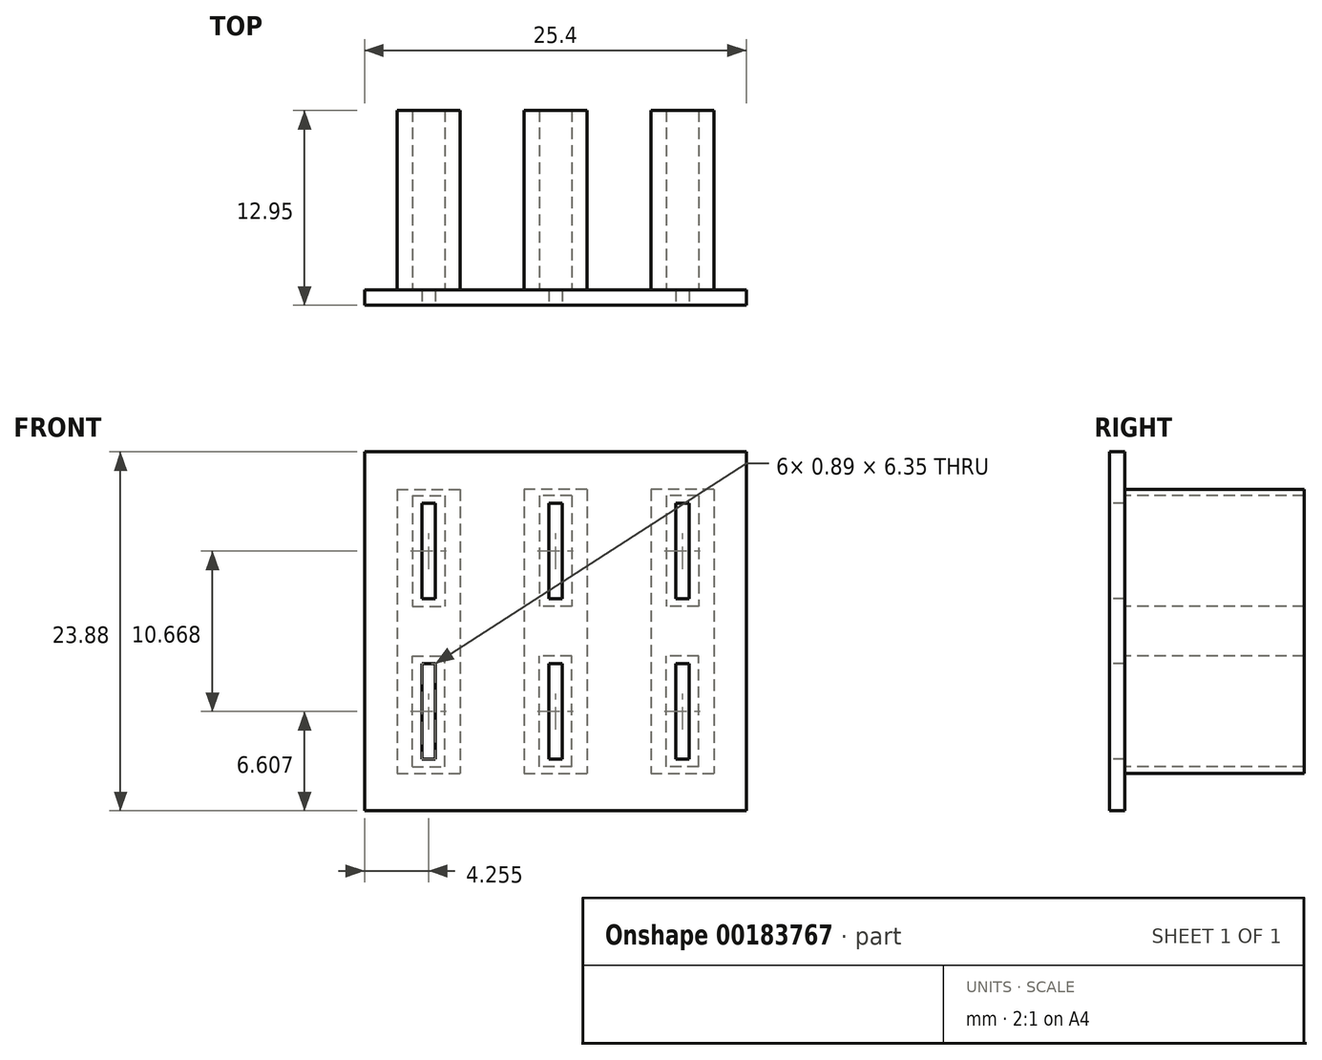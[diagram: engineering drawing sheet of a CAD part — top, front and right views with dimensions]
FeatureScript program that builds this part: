
annotation { "Feature Type Name" : "Feature", "Feature Type Description" : "" }
export const myFeature = defineFeature(function(context is Context, id is Id, definition is map)
    precondition{}
    {
        {
            var Q0;
            Q0=qCreatedBy(makeId("Front.planeOp"),FACE);
            var sketch = newSketch(context, id + "F0", { "sketchPlane" : qUnion([Q0])});
            skLineSegment(sketch, "E0.bottom", {"start": v(-12.7, 12.4) * mm, "end": v(12.7, 12.4) * mm});
            skLineSegment(sketch, "E0.top", {"start": v(-12.7, -11.47) * mm, "end": v(12.7, -11.47) * mm});
            skLineSegment(sketch, "E0.left", {"start": v(-12.7, 12.4) * mm, "end": v(-12.7, -11.47) * mm});
            skLineSegment(sketch, "E0.right", {"start": v(12.7, 12.4) * mm, "end": v(12.7, -11.47) * mm});
            skPoint(sketch, "E0.middle", {"position": v(0, 0.47) * mm});
            skLineSegment(sketch, "E1", {"start": v(0, 12.4) * mm, "end": v(0, -11.47) * mm, "construction": true});
            skLineSegment(sketch, "E2", {"start": v(0, 12.4) * mm, "end": v(-12.7, 12.4) * mm, "construction": true});
            skLineSegment(sketch, "E3", {"start": v(-8.45, 12.4) * mm, "end": v(-8.45, -11.47) * mm, "construction": true});
            skLineSegment(sketch, "E4.MirrorCS", {"start": v(8.45, 12.4) * mm, "end": v(8.45, -11.47) * mm, "construction": true});
            skLineSegment(sketch, "E5", {"start": v(-12.7, 0.47) * mm, "end": v(12.7, 0.47) * mm, "construction": true});
            skLineSegment(sketch, "E6.bottom", {"start": v(-8, 8.98) * mm, "end": v(-8.89, 8.98) * mm});
            skLineSegment(sketch, "E6.top", {"start": v(-8, 2.63) * mm, "end": v(-8.89, 2.63) * mm});
            skLineSegment(sketch, "E6.left", {"start": v(-8, 8.98) * mm, "end": v(-8, 2.63) * mm});
            skLineSegment(sketch, "E6.right", {"start": v(-8.9, 8.98) * mm, "end": v(-8.9, 2.63) * mm});
            skPoint(sketch, "E6.middle", {"position": v(-8.45, 5.8) * mm});
            skLineSegment(sketch, "E7.MirrorCS", {"start": v(8, 8.98) * mm, "end": v(8, 2.63) * mm});
            skLineSegment(sketch, "E8.MirrorCS", {"start": v(8, 8.98) * mm, "end": v(8.89, 8.98) * mm});
            skLineSegment(sketch, "E9.MirrorCS", {"start": v(8.9, 8.98) * mm, "end": v(8.9, 2.63) * mm});
            skLineSegment(sketch, "E10.MirrorCS", {"start": v(8, 2.63) * mm, "end": v(8.89, 2.63) * mm});
            skLineSegment(sketch, "E11", {"start": v(0, 12.4) * mm, "end": v(-8.45, 12.4) * mm});
            skLineSegment(sketch, "E12", {"start": v(-4.22, 12.4) * mm, "end": v(-4.22, -11.47) * mm, "construction": true});
            skLineSegment(sketch, "E13.MirrorCS", {"start": v(4.22, 12.4) * mm, "end": v(4.22, -11.47) * mm, "construction": true});
            skPoint(sketch, "E14.MirrorP", {"position": v(0, 5.8) * mm});
            skLineSegment(sketch, "E15.MirrorCS", {"start": v(0.44, 8.98) * mm, "end": v(0.44, 2.63) * mm});
            skLineSegment(sketch, "E16.MirrorCS", {"start": v(-0.44, 8.98) * mm, "end": v(-0.44, 2.63) * mm});
            skLineSegment(sketch, "E17.MirrorCS", {"start": v(-0.44, 2.63) * mm, "end": v(0.44, 2.63) * mm});
            skLineSegment(sketch, "E18.MirrorCS", {"start": v(-0.44, 8.98) * mm, "end": v(0.44, 8.98) * mm});
            skLineSegment(sketch, "E19.MirrorCS", {"start": v(8, -1.69) * mm, "end": v(8.9, -1.69) * mm});
            skLineSegment(sketch, "E20.MirrorCS", {"start": v(-0.44, -8.04) * mm, "end": v(-0.44, -1.69) * mm});
            skLineSegment(sketch, "E21.MirrorCS", {"start": v(-0.44, -1.69) * mm, "end": v(0.44, -1.69) * mm});
            skLineSegment(sketch, "E22.MirrorCS", {"start": v(-8.9, -8.04) * mm, "end": v(-8.9, -1.69) * mm});
            skLineSegment(sketch, "E23.MirrorCS", {"start": v(-8, -8.04) * mm, "end": v(-8, -1.69) * mm});
            skLineSegment(sketch, "E24.MirrorCS", {"start": v(-8, -1.69) * mm, "end": v(-8.89, -1.69) * mm});
            skLineSegment(sketch, "E25.MirrorCS", {"start": v(-8, -8.04) * mm, "end": v(-8.89, -8.04) * mm});
            skPoint(sketch, "E26.MirrorP", {"position": v(-8.45, -4.86) * mm});
            skLineSegment(sketch, "E27.MirrorCS", {"start": v(-0.44, -8.04) * mm, "end": v(0.44, -8.04) * mm});
            skLineSegment(sketch, "E28.MirrorCS", {"start": v(0.44, -8.04) * mm, "end": v(0.44, -1.69) * mm});
            skLineSegment(sketch, "E29.MirrorCS", {"start": v(8, -8.04) * mm, "end": v(8, -1.69) * mm});
            skLineSegment(sketch, "E30.MirrorCS", {"start": v(8, -8.04) * mm, "end": v(8.89, -8.04) * mm});
            skPoint(sketch, "E31.MirrorP", {"position": v(0, -4.86) * mm});
            skLineSegment(sketch, "E32.MirrorCS", {"start": v(8.9, -8.04) * mm, "end": v(8.9, -1.69) * mm});
            skLineSegment(sketch, "E33.bottom", {"start": v(-9.52, 9.49) * mm, "end": v(-7.37, 9.49) * mm});
            skLineSegment(sketch, "E33.top", {"start": v(-9.52, 2.12) * mm, "end": v(-7.37, 2.12) * mm});
            skLineSegment(sketch, "E33.left", {"start": v(-9.53, 9.49) * mm, "end": v(-9.53, 2.12) * mm});
            skLineSegment(sketch, "E33.right", {"start": v(-7.37, 9.49) * mm, "end": v(-7.37, 2.12) * mm});
            skLineSegment(sketch, "E34.top", {"start": v(-6.35, 0.47) * mm, "end": v(-10.54, 0.47) * mm});
            skLineSegment(sketch, "E35", {"start": v(-10.54, 9.9) * mm, "end": v(-6.35, 9.9) * mm});
            skLineSegment(sketch, "E36.bottom", {"start": v(-6.35, 9.9) * mm, "end": v(-10.54, 9.9) * mm});
            skLineSegment(sketch, "E36.left", {"start": v(-6.35, 9.9) * mm, "end": v(-6.35, 0.47) * mm});
            skLineSegment(sketch, "E36.right", {"start": v(-10.54, 9.9) * mm, "end": v(-10.54, 0.47) * mm});
            skLineSegment(sketch, "E37.MirrorCS", {"start": v(-2.1, 0.47) * mm, "end": v(2.1, 0.47) * mm});
            skLineSegment(sketch, "E38.MirrorCS", {"start": v(2.1, 9.9) * mm, "end": v(-2.1, 9.9) * mm});
            skLineSegment(sketch, "E39.MirrorCS", {"start": v(1.08, 9.49) * mm, "end": v(-1.08, 9.49) * mm});
            skLineSegment(sketch, "E40.MirrorCS", {"start": v(2.1, 9.9) * mm, "end": v(2.1, 0.47) * mm});
            skLineSegment(sketch, "E41.MirrorCS", {"start": v(-1.08, 9.49) * mm, "end": v(-1.08, 2.12) * mm});
            skLineSegment(sketch, "E42.MirrorCS", {"start": v(-2.1, 9.9) * mm, "end": v(-2.1, 0.47) * mm});
            skLineSegment(sketch, "E43.MirrorCS", {"start": v(1.08, 9.49) * mm, "end": v(1.08, 2.12) * mm});
            skLineSegment(sketch, "E44.MirrorCS", {"start": v(-2.1, 9.9) * mm, "end": v(2.1, 9.9) * mm});
            skLineSegment(sketch, "E45.MirrorCS", {"start": v(1.08, 2.12) * mm, "end": v(-1.08, 2.12) * mm});
            skPoint(sketch, "E46.MirrorP", {"position": v(8.45, 5.8) * mm});
            skLineSegment(sketch, "E47.MirrorCS", {"start": v(6.35, 0.47) * mm, "end": v(10.54, 0.47) * mm});
            skLineSegment(sketch, "E48.MirrorCS", {"start": v(10.54, 9.9) * mm, "end": v(6.35, 9.9) * mm});
            skLineSegment(sketch, "E49.MirrorCS", {"start": v(7.37, 9.49) * mm, "end": v(7.37, 2.12) * mm});
            skLineSegment(sketch, "E50.MirrorCS", {"start": v(6.35, 9.9) * mm, "end": v(10.54, 9.9) * mm});
            skLineSegment(sketch, "E51.MirrorCS", {"start": v(9.53, 9.49) * mm, "end": v(9.53, 2.12) * mm});
            skLineSegment(sketch, "E52.MirrorCS", {"start": v(6.35, 9.9) * mm, "end": v(6.35, 0.47) * mm});
            skLineSegment(sketch, "E53.MirrorCS", {"start": v(10.54, 9.9) * mm, "end": v(10.54, 0.47) * mm});
            skLineSegment(sketch, "E54.MirrorCS", {"start": v(9.52, 2.12) * mm, "end": v(7.37, 2.12) * mm});
            skLineSegment(sketch, "E55.MirrorCS", {"start": v(9.52, 9.49) * mm, "end": v(7.37, 9.49) * mm});
            skPoint(sketch, "E56.MirrorP", {"position": v(8.45, -4.86) * mm});
            skLineSegment(sketch, "E57.MirrorCS", {"start": v(6.35, -8.97) * mm, "end": v(10.54, -8.97) * mm});
            skLineSegment(sketch, "E58.MirrorCS", {"start": v(-10.54, -8.97) * mm, "end": v(-6.35, -8.97) * mm});
            skLineSegment(sketch, "E59.MirrorCS", {"start": v(-2.1, -8.97) * mm, "end": v(2.1, -8.97) * mm});
            skLineSegment(sketch, "E60.MirrorCS", {"start": v(10.54, -8.97) * mm, "end": v(10.54, 0.47) * mm});
            skLineSegment(sketch, "E61.MirrorCS", {"start": v(-9.52, -8.55) * mm, "end": v(-7.37, -8.55) * mm});
            skLineSegment(sketch, "E62.MirrorCS", {"start": v(-9.53, -8.55) * mm, "end": v(-9.53, -1.18) * mm});
            skLineSegment(sketch, "E63.MirrorCS", {"start": v(6.35, -8.97) * mm, "end": v(6.35, 0.47) * mm});
            skLineSegment(sketch, "E64.MirrorCS", {"start": v(-10.54, -8.97) * mm, "end": v(-10.54, 0.47) * mm});
            skLineSegment(sketch, "E65.MirrorCS", {"start": v(1.08, -8.55) * mm, "end": v(1.08, -1.18) * mm});
            skLineSegment(sketch, "E66.MirrorCS", {"start": v(10.54, -8.97) * mm, "end": v(6.35, -8.97) * mm});
            skLineSegment(sketch, "E67.MirrorCS", {"start": v(-7.37, -8.55) * mm, "end": v(-7.37, -1.18) * mm});
            skLineSegment(sketch, "E68.MirrorCS", {"start": v(9.53, -8.55) * mm, "end": v(9.53, -1.18) * mm});
            skLineSegment(sketch, "E69.MirrorCS", {"start": v(-6.35, -8.97) * mm, "end": v(-6.35, 0.47) * mm});
            skLineSegment(sketch, "E70.MirrorCS", {"start": v(-2.1, -8.97) * mm, "end": v(-2.1, 0.47) * mm});
            skLineSegment(sketch, "E71.MirrorCS", {"start": v(-6.35, -8.97) * mm, "end": v(-10.54, -8.97) * mm});
            skLineSegment(sketch, "E72.MirrorCS", {"start": v(1.08, -8.55) * mm, "end": v(-1.08, -8.55) * mm});
            skLineSegment(sketch, "E73.MirrorCS", {"start": v(2.1, -8.97) * mm, "end": v(2.1, 0.47) * mm});
            skLineSegment(sketch, "E74.MirrorCS", {"start": v(-1.08, -8.55) * mm, "end": v(-1.08, -1.18) * mm});
            skLineSegment(sketch, "E75.MirrorCS", {"start": v(7.37, -8.55) * mm, "end": v(7.37, -1.18) * mm});
            skLineSegment(sketch, "E76.MirrorCS", {"start": v(9.52, -1.18) * mm, "end": v(7.37, -1.18) * mm});
            skLineSegment(sketch, "E77.MirrorCS", {"start": v(2.1, -8.97) * mm, "end": v(-2.1, -8.97) * mm});
            skLineSegment(sketch, "E78.MirrorCS", {"start": v(1.08, -1.18) * mm, "end": v(-1.08, -1.18) * mm});
            skLineSegment(sketch, "E79.MirrorCS", {"start": v(-9.52, -1.18) * mm, "end": v(-7.37, -1.18) * mm});
            skLineSegment(sketch, "E80.MirrorCS", {"start": v(9.52, -8.55) * mm, "end": v(7.37, -8.55) * mm});
            skSolve(sketch);
        }
        {
            var Q0;
            Q0 = qSketchRegion(id + "F0", true);
            var Q1;
            Q1=makeQuery(id+"F0.imprint","IMPRINT",FACE,{"disambiguationData":[TD([[makeQuery(id+"F0.imprint","IMPRINT",EDGE,{"derivedFrom":sQuery(id+"F0.wireOp",EDGE,"E33.bottom")}),1.0]])]});
            var Q2;
            Q2=makeQuery(id+"F0.imprint","IMPRINT",FACE,{"disambiguationData":[TD([[makeQuery(id+"F0.imprint","IMPRINT",EDGE,{"derivedFrom":sQuery(id+"F0.wireOp",EDGE,"E6.bottom")}),-1.0]])]});
            var Q3;
            Q3=makeQuery(id+"F0.imprint","IMPRINT",FACE,{"disambiguationData":[TD([[makeQuery(id+"F0.imprint","IMPRINT",EDGE,{"derivedFrom":sQuery(id+"F0.wireOp",EDGE,"E39.MirrorCS")}),-1.0]])]});
            var Q4;
            Q4=makeQuery(id+"F0.imprint","IMPRINT",FACE,{"disambiguationData":[TD([[makeQuery(id+"F0.imprint","IMPRINT",EDGE,{"derivedFrom":sQuery(id+"F0.wireOp",EDGE,"E39.MirrorCS")}),1.0]])]});
            var Q5;
            Q5=makeQuery(id+"F0.imprint","IMPRINT",FACE,{"disambiguationData":[TD([[makeQuery(id+"F0.imprint","IMPRINT",EDGE,{"derivedFrom":sQuery(id+"F0.wireOp",EDGE,"E65.MirrorCS")}),-1.0]])]});
            var Q6;
            Q6=makeQuery(id+"F0.imprint","IMPRINT",FACE,{"disambiguationData":[TD([[makeQuery(id+"F0.imprint","IMPRINT",EDGE,{"derivedFrom":sQuery(id+"F0.wireOp",EDGE,"E27.MirrorCS")}),-1.0]])]});
            var Q7;
            Q7=makeQuery(id+"F0.imprint","IMPRINT",FACE,{"disambiguationData":[TD([[makeQuery(id+"F0.imprint","IMPRINT",EDGE,{"derivedFrom":sQuery(id+"F0.wireOp",EDGE,"E61.MirrorCS")}),-1.0]])]});
            var Q8;
            Q8=makeQuery(id+"F0.imprint","IMPRINT",FACE,{"disambiguationData":[TD([[makeQuery(id+"F0.imprint","IMPRINT",EDGE,{"derivedFrom":sQuery(id+"F0.wireOp",EDGE,"E61.MirrorCS")}),1.0]])]});
            var Q9;
            Q9=makeQuery(id+"F0.imprint","IMPRINT",FACE,{"disambiguationData":[TD([[makeQuery(id+"F0.imprint","IMPRINT",EDGE,{"derivedFrom":sQuery(id+"F0.wireOp",EDGE,"E60.MirrorCS")}),1.0]])]});
            var Q10;
            Q10=makeQuery(id+"F0.imprint","IMPRINT",FACE,{"disambiguationData":[TD([[makeQuery(id+"F0.imprint","IMPRINT",EDGE,{"derivedFrom":sQuery(id+"F0.wireOp",EDGE,"E68.MirrorCS")}),1.0]])]});
            var Q11;
            Q11=makeQuery(id+"F0.imprint","IMPRINT",FACE,{"disambiguationData":[TD([[makeQuery(id+"F0.imprint","IMPRINT",EDGE,{"derivedFrom":sQuery(id+"F0.wireOp",EDGE,"E49.MirrorCS")}),-1.0]])]});
            var Q12;
            Q12=makeQuery(id+"F0.imprint","IMPRINT",FACE,{"disambiguationData":[TD([[makeQuery(id+"F0.imprint","IMPRINT",EDGE,{"derivedFrom":sQuery(id+"F0.wireOp",EDGE,"E49.MirrorCS")}),1.0]])]});
            extrude(context, id + "F1", {"entities" : qUnion([Q0, Q1, Q2, Q3, Q4, Q5, Q6, Q7, Q8, Q9, Q10, Q11, Q12]), "oppositeDirection" : true, "depth" : 1.02 * mm});
        }
        {
            var Q0;
            Q0=makeQuery(id+"F0.imprint","IMPRINT",FACE,{"disambiguationData":[TD([[makeQuery(id+"F0.imprint","IMPRINT",EDGE,{"derivedFrom":sQuery(id+"F0.wireOp",EDGE,"E33.bottom")}),1.0]])]});
            var Q1;
            Q1=makeQuery(id+"F0.imprint","IMPRINT",FACE,{"disambiguationData":[TD([[makeQuery(id+"F0.imprint","IMPRINT",EDGE,{"derivedFrom":sQuery(id+"F0.wireOp",EDGE,"E61.MirrorCS")}),-1.0]])]});
            var Q2;
            Q2=makeQuery(id+"F0.imprint","IMPRINT",FACE,{"disambiguationData":[TD([[makeQuery(id+"F0.imprint","IMPRINT",EDGE,{"derivedFrom":sQuery(id+"F0.wireOp",EDGE,"E39.MirrorCS")}),-1.0]])]});
            var Q3;
            Q3=makeQuery(id+"F0.imprint","IMPRINT",FACE,{"disambiguationData":[TD([[makeQuery(id+"F0.imprint","IMPRINT",EDGE,{"derivedFrom":sQuery(id+"F0.wireOp",EDGE,"E65.MirrorCS")}),-1.0]])]});
            var Q4;
            Q4=makeQuery(id+"F0.imprint","IMPRINT",FACE,{"disambiguationData":[TD([[makeQuery(id+"F0.imprint","IMPRINT",EDGE,{"derivedFrom":sQuery(id+"F0.wireOp",EDGE,"E49.MirrorCS")}),-1.0]])]});
            var Q5;
            Q5=makeQuery(id+"F0.imprint","IMPRINT",FACE,{"disambiguationData":[TD([[makeQuery(id+"F0.imprint","IMPRINT",EDGE,{"derivedFrom":sQuery(id+"F0.wireOp",EDGE,"E60.MirrorCS")}),1.0]])]});
            extrude(context, id + "F2", {"entities" : qUnion([Q0, Q1, Q2, Q3, Q4, Q5]), "operationType" : NewBodyOperationType.ADD, "oppositeDirection" : true, "depth" : 12.95 * mm});
        }
    });
